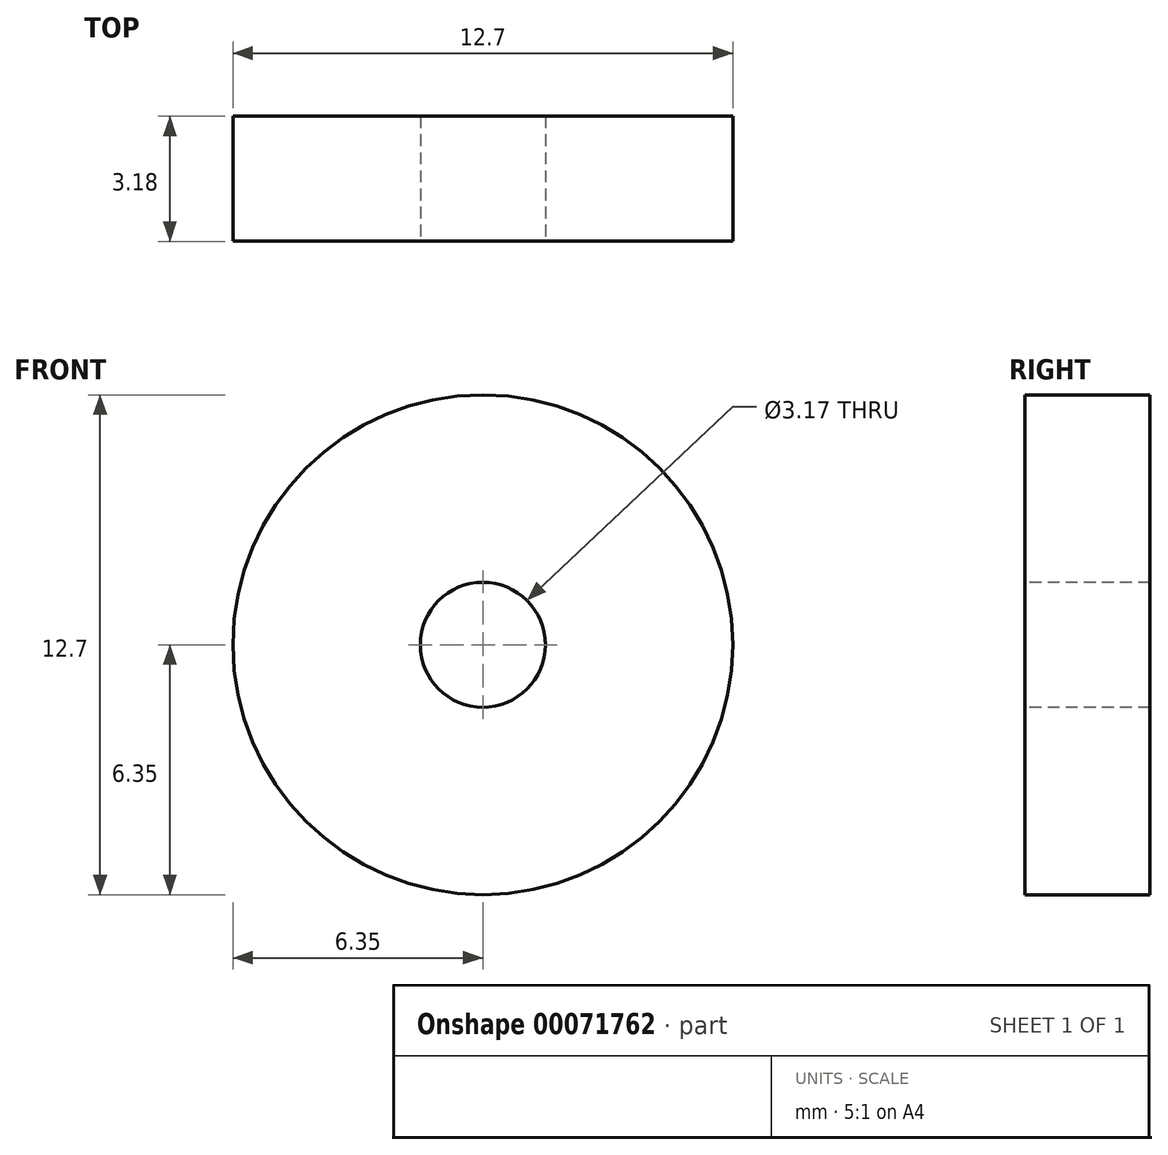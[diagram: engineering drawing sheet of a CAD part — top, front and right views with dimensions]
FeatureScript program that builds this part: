
annotation { "Feature Type Name" : "Feature", "Feature Type Description" : "" }
export const myFeature = defineFeature(function(context is Context, id is Id, definition is map)
    precondition{}
    {
        {
            var Q0;
            Q0=qCreatedBy(makeId("Front.planeOp"),FACE);
            var sketch = newSketch(context, id + "F0", { "sketchPlane" : qUnion([Q0])});
            skCircle(sketch, "E0", {"center": v(0, 0) * mm, "radius": 6.35 * mm});
            skSolve(sketch);
        }
        {
            var Q0;
            Q0 = qSketchRegion(id + "F0", true);
            extrude(context, id + "F1", {"entities" : qUnion([Q0]), "depth" : 3.17 * mm});
        }
        {
            var Q0;
            Q0=makeQuery(id+"F1.opExtrude","CAP_FACE",FACE,{"disambiguationData":[OSD([sQuery(id+"F0.wireOp",EDGE,"E0")])],"isStart":false});
            var sketch = newSketch(context, id + "F2", { "sketchPlane" : qUnion([Q0])});
            skCircle(sketch, "E1.0", {"center": v(0, 0) * mm, "radius": 6.35 * mm});
            skCircle(sketch, "E2", {"center": v(0, 0) * mm, "radius": 1.59 * mm});
            skSolve(sketch);
        }
        {
            var Q0;
            Q0=makeQuery(id+"F2.imprint","IMPRINT",FACE,{"disambiguationData":[TD([[makeQuery(id+"F2.imprint","IMPRINT",EDGE,{"derivedFrom":sQuery(id+"F2.wireOp",EDGE,"E2")}),1.0]])]});
            extrude(context, id + "F3", {"entities" : qUnion([Q0]), "operationType" : NewBodyOperationType.REMOVE, "endBound" : BoundingType.THROUGH_ALL, "oppositeDirection" : true, "depth" : 25.4 * mm});
        }
    });
